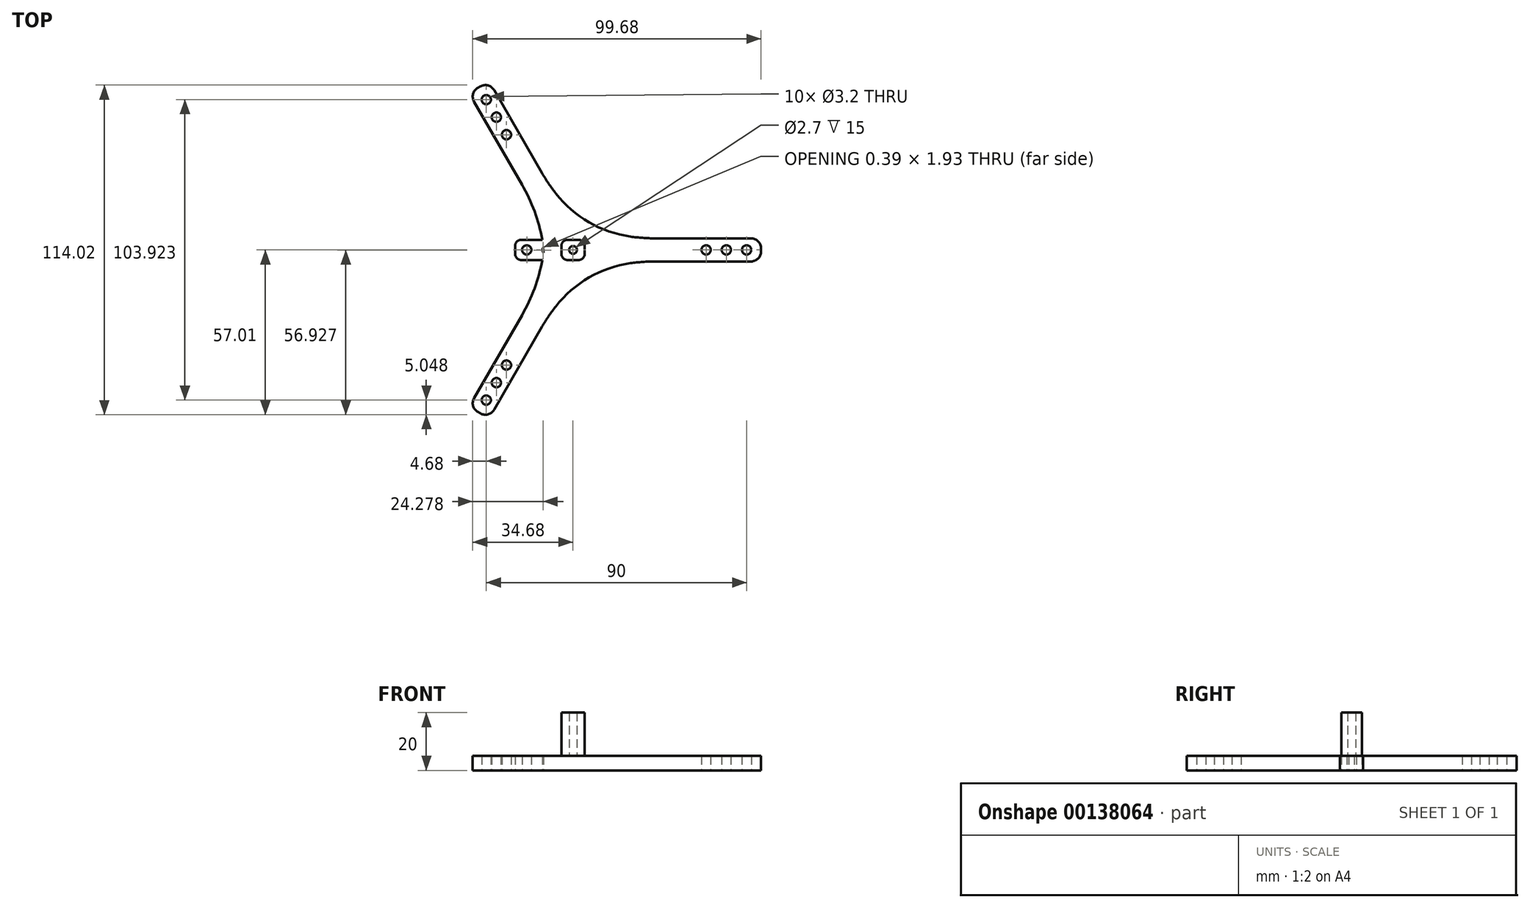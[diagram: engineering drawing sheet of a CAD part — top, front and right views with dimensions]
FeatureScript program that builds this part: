
annotation { "Feature Type Name" : "Feature", "Feature Type Description" : "" }
export const myFeature = defineFeature(function(context is Context, id is Id, definition is map)
    precondition{}
    {
        {
            var Q0;
            Q0=qCreatedBy(makeId("Top.planeOp"),FACE);
            var sketch = newSketch(context, id + "F0", { "sketchPlane" : qUnion([Q0])});
            skLineSegment(sketch, "E0.bottom", {"start": v(20, -3.5) * mm, "end": v(-20, -3.5) * mm});
            skLineSegment(sketch, "E0.top", {"start": v(20, 3.5) * mm, "end": v(-20, 3.5) * mm});
            skLineSegment(sketch, "E0.left", {"start": v(20, -3.5) * mm, "end": v(20, 3.5) * mm});
            skLineSegment(sketch, "E0.right", {"start": v(-20, -3.5) * mm, "end": v(-20, 3.5) * mm});
            skPoint(sketch, "E0.middle", {"position": v(0, 0) * mm});
            skLineSegment(sketch, "E1", {"start": v(-16, 0) * mm, "end": v(-9, 0) * mm, "construction": true});
            skLineSegment(sketch, "E2", {"start": v(-9, 0) * mm, "end": v(0, 0) * mm, "construction": true});
            skLineSegment(sketch, "E3", {"start": v(0, 0) * mm, "end": v(9, 0) * mm, "construction": true});
            skLineSegment(sketch, "E4", {"start": v(9, 0) * mm, "end": v(16, 0) * mm, "construction": true});
            skCircle(sketch, "E5", {"center": v(-16, 0) * mm, "radius": 1.6 * mm});
            skCircle(sketch, "E6", {"center": v(-9, 0) * mm, "radius": 1.6 * mm});
            skCircle(sketch, "E7", {"center": v(9, 0) * mm, "radius": 1.6 * mm});
            skCircle(sketch, "E8", {"center": v(16, 0) * mm, "radius": 1.6 * mm});
            skCircle(sketch, "E9", {"center": v(0, 0) * mm, "radius": 1.35 * mm});
            skSolve(sketch);
        }
        {
            var Q0;
            Q0 = qSketchRegion(id + "F0", true);
            extrude(context, id + "F1", {"entities" : qUnion([Q0]), "depth" : 5 * mm});
        }
        {
            var Q0;
            Q0=qCreatedBy(makeId("Top.planeOp"),FACE);
            var sketch = newSketch(context, id + "F2", { "sketchPlane" : qUnion([Q0])});
            skLineSegment(sketch, "E10.bottom", {"start": v(4, -3.5) * mm, "end": v(-4, -3.5) * mm});
            skLineSegment(sketch, "E10.top", {"start": v(4, 3.5) * mm, "end": v(-4, 3.5) * mm});
            skLineSegment(sketch, "E10.left", {"start": v(4, -3.5) * mm, "end": v(4, 3.5) * mm});
            skLineSegment(sketch, "E10.right", {"start": v(-4, -3.5) * mm, "end": v(-4, 3.5) * mm});
            skPoint(sketch, "E10.middle", {"position": v(0, 0) * mm});
            skCircle(sketch, "E11", {"center": v(0, 0) * mm, "radius": 1.35 * mm});
            skSolve(sketch);
        }
        {
            var Q0;
            Q0 = qSketchRegion(id + "F2", true);
            extrude(context, id + "F3", {"entities" : qUnion([Q0]), "operationType" : NewBodyOperationType.ADD, "depth" : 20 * mm});
        }
        {
            var Q0;
            Q0=makeQuery(id+"F1.opExtrude","SWEPT_EDGE",EDGE,{"disambiguationData":[OSD([sQuery(id+"F0.wireOp",EDGE,"E0.bottom"),sQuery(id+"F0.wireOp",EDGE,"E0.right")])]});
            var Q1;
            Q1=makeQuery(id+"F1.opExtrude","SWEPT_EDGE",EDGE,{"disambiguationData":[OSD([sQuery(id+"F0.wireOp",EDGE,"E0.top"),sQuery(id+"F0.wireOp",EDGE,"E0.right")])]});
            var Q2;
            Q2=makeQuery(id+"F1.opExtrude","SWEPT_EDGE",EDGE,{"disambiguationData":[OSD([sQuery(id+"F0.wireOp",EDGE,"E0.bottom"),sQuery(id+"F0.wireOp",EDGE,"E0.left")])]});
            var Q3;
            Q3=makeQuery(id+"F3.opExtrude","SWEPT_EDGE",EDGE,{"disambiguationData":[OSD([sQuery(id+"F2.wireOp",EDGE,"E10.bottom"),sQuery(id+"F2.wireOp",EDGE,"E10.right")])]});
            var Q4;
            Q4=makeQuery(id+"F3.opExtrude","SWEPT_EDGE",EDGE,{"disambiguationData":[OSD([sQuery(id+"F2.wireOp",EDGE,"E10.bottom"),sQuery(id+"F2.wireOp",EDGE,"E10.left")])]});
            var Q5;
            Q5=makeQuery(id+"F3.opExtrude","SWEPT_EDGE",EDGE,{"disambiguationData":[OSD([sQuery(id+"F2.wireOp",EDGE,"E10.top"),sQuery(id+"F2.wireOp",EDGE,"E10.right")])]});
            var Q6;
            Q6=makeQuery(id+"F1.opExtrude","SWEPT_EDGE",EDGE,{"disambiguationData":[OSD([sQuery(id+"F0.wireOp",EDGE,"E0.top"),sQuery(id+"F0.wireOp",EDGE,"E0.left")])]});
            var Q7;
            Q7=makeQuery(id+"F3.opExtrude","SWEPT_EDGE",EDGE,{"disambiguationData":[OSD([sQuery(id+"F2.wireOp",EDGE,"E10.top"),sQuery(id+"F2.wireOp",EDGE,"E10.left")])]});
            fillet(context, id + "F4", {"entities" : qUnion([Q0, Q1, Q2, Q3, Q4, Q5, Q6, Q7]), "radius" : 2 * mm, "tangentPropagation" : true, "allowEdgeOverflow" : false});
        }
        {
            var Q0;
            Q0=qCreatedBy(makeId("Top.planeOp"),FACE);
            var sketch = newSketch(context, id + "F5", { "sketchPlane" : qUnion([Q0])});
            skCircle(sketch, "E12", {"center": v(0, 0) * mm, "radius": 60 * mm, "construction": true});
            skLineSegment(sketch, "E13.bottom", {"start": v(0, 4) * mm, "end": v(65, 4) * mm});
            skLineSegment(sketch, "E13.top", {"start": v(0, -4) * mm, "end": v(65, -4) * mm});
            skLineSegment(sketch, "E13.left", {"start": v(0, 4) * mm, "end": v(0, -4) * mm});
            skLineSegment(sketch, "E13.right", {"start": v(65, 4) * mm, "end": v(65, -4) * mm});
            skCircle(sketch, "E14", {"center": v(60, 0) * mm, "radius": 1.6 * mm});
            skLineSegment(sketch, "E15", {"start": v(0, 0) * mm, "end": v(46, 0) * mm, "construction": true});
            skLineSegment(sketch, "E16", {"start": v(46, 0) * mm, "end": v(53, 0) * mm, "construction": true});
            skLineSegment(sketch, "E17", {"start": v(53, 0) * mm, "end": v(60, 0) * mm, "construction": true});
            skCircle(sketch, "E18", {"center": v(53, 0) * mm, "radius": 1.6 * mm});
            skCircle(sketch, "E19", {"center": v(46, 0) * mm, "radius": 1.6 * mm});
            skCircle(sketch, "E20", {"center": v(0, 0) * mm, "radius": 10 * mm});
            skSolve(sketch);
        }
        {
            var Q0;
            Q0 = qSketchRegion(id + "F5", true);
            extrude(context, id + "F6", {"entities" : qUnion([Q0]), "depth" : 5 * mm});
        }
        {
            var Q0;
            Q0=makeQuery(id+"F6.opExtrude","SWEPT_EDGE",EDGE,{"disambiguationData":[OSD([sQuery(id+"F5.wireOp",EDGE,"E13.top"),sQuery(id+"F5.wireOp",EDGE,"E20")])]});
            var Q1;
            Q1=makeQuery(id+"F6.opExtrude","SWEPT_EDGE",EDGE,{"disambiguationData":[OSD([sQuery(id+"F5.wireOp",EDGE,"E13.bottom"),sQuery(id+"F5.wireOp",EDGE,"E20")])]});
            fillet(context, id + "F7", {"entities" : qUnion([Q0, Q1]), "radius" : 60 * mm, "tangentPropagation" : true, "allowEdgeOverflow" : false});
        }
        {
            var Q0;
            Q0=makeQuery(id+"F6.opExtrude","SWEPT_EDGE",EDGE,{"disambiguationData":[OSD([sQuery(id+"F5.wireOp",EDGE,"E13.top"),sQuery(id+"F5.wireOp",EDGE,"E13.right")])]});
            var Q1;
            Q1=makeQuery(id+"F6.opExtrude","SWEPT_EDGE",EDGE,{"disambiguationData":[OSD([sQuery(id+"F5.wireOp",EDGE,"E13.bottom"),sQuery(id+"F5.wireOp",EDGE,"E13.right")])]});
            fillet(context, id + "F8", {"entities" : qUnion([Q0, Q1]), "radius" : 3.5 * mm, "tangentPropagation" : true, "allowEdgeOverflow" : false});
        }
        {
            var Q0;
            Q0=qCreatedBy(makeId("Right.planeOp"),FACE);
            var sketch = newSketch(context, id + "F9", { "sketchPlane" : qUnion([Q0])});
            skLineSegment(sketch, "E21", {"start": v(0, 0) * mm, "end": v(0, 19.21) * mm, "construction": true});
            skSolve(sketch);
        }
        {
            var Q0;
            Q0=makeQuery(id+"F6.opExtrude","SWEPT_BODY",BODY,{"disambiguationData":[OSD([sQuery(id+"F5.wireOp",EDGE,"E13.bottom"),sQuery(id+"F5.wireOp",EDGE,"E13.top"),sQuery(id+"F5.wireOp",EDGE,"E13.right"),sQuery(id+"F5.wireOp",EDGE,"E14"),sQuery(id+"F5.wireOp",EDGE,"E18"),sQuery(id+"F5.wireOp",EDGE,"E19"),sQuery(id+"F5.wireOp",EDGE,"E20")])]});
            var Q1;
            Q1=sQuery(id+"F9.wireOp",EDGE,"E21");
            circularPattern(context, id + "F10", {"operationType" : NewBodyOperationType.ADD, "entities" : qUnion([Q0]), "axis" : qUnion([Q1]), "angle" : 360 * degree, "instanceCount" : 3, "equalSpace" : true});
        }
        {
            var Q0;
            {var subQ0=sQuery(id+"F5.wireOp",EDGE,"E20");Q0=makeQuery(id+"F10.boolean.opBoolean","INTERSECT",EDGE,{"derivedFrom":[makeQuery(id+"F7.opFillet","BLEND_FACE",FACE,{"disambiguationData":[OSD([sQuery(id+"F5.wireOp",EDGE,"E13.top"),subQ0])]}),makeQuery(id+"F10.opPattern","COPY",FACE,{"derivedFrom":makeQuery(id+"F7.opFillet","BLEND_FACE",FACE,{"disambiguationData":[OSD([sQuery(id+"F5.wireOp",EDGE,"E13.bottom"),subQ0])]}),"instanceName":"2"})]});}
            var Q1;
            {var subQ0=sQuery(id+"F5.wireOp",EDGE,"E20");Q1=makeQuery(id+"F10.boolean.opBoolean","INTERSECT",EDGE,{"derivedFrom":[makeQuery(id+"F10.opPattern","COPY",FACE,{"derivedFrom":makeQuery(id+"F7.opFillet","BLEND_FACE",FACE,{"disambiguationData":[OSD([sQuery(id+"F5.wireOp",EDGE,"E13.bottom"),subQ0])]}),"instanceName":"1"}),makeQuery(id+"F10.opPattern","COPY",FACE,{"derivedFrom":makeQuery(id+"F7.opFillet","BLEND_FACE",FACE,{"disambiguationData":[OSD([sQuery(id+"F5.wireOp",EDGE,"E13.top"),subQ0])]}),"instanceName":"2"})]});}
            var Q2;
            {var subQ0=sQuery(id+"F5.wireOp",EDGE,"E20");Q2=makeQuery(id+"F10.boolean.opBoolean","INTERSECT",EDGE,{"derivedFrom":[makeQuery(id+"F7.opFillet","BLEND_FACE",FACE,{"disambiguationData":[OSD([sQuery(id+"F5.wireOp",EDGE,"E13.bottom"),subQ0])]}),makeQuery(id+"F10.opPattern","COPY",FACE,{"derivedFrom":makeQuery(id+"F7.opFillet","BLEND_FACE",FACE,{"disambiguationData":[OSD([sQuery(id+"F5.wireOp",EDGE,"E13.top"),subQ0])]}),"instanceName":"1"})]});}
            fillet(context, id + "F11", {"entities" : qUnion([Q0, Q1, Q2]), "radius" : 40 * mm, "tangentPropagation" : true, "allowEdgeOverflow" : false});
        }
    });
